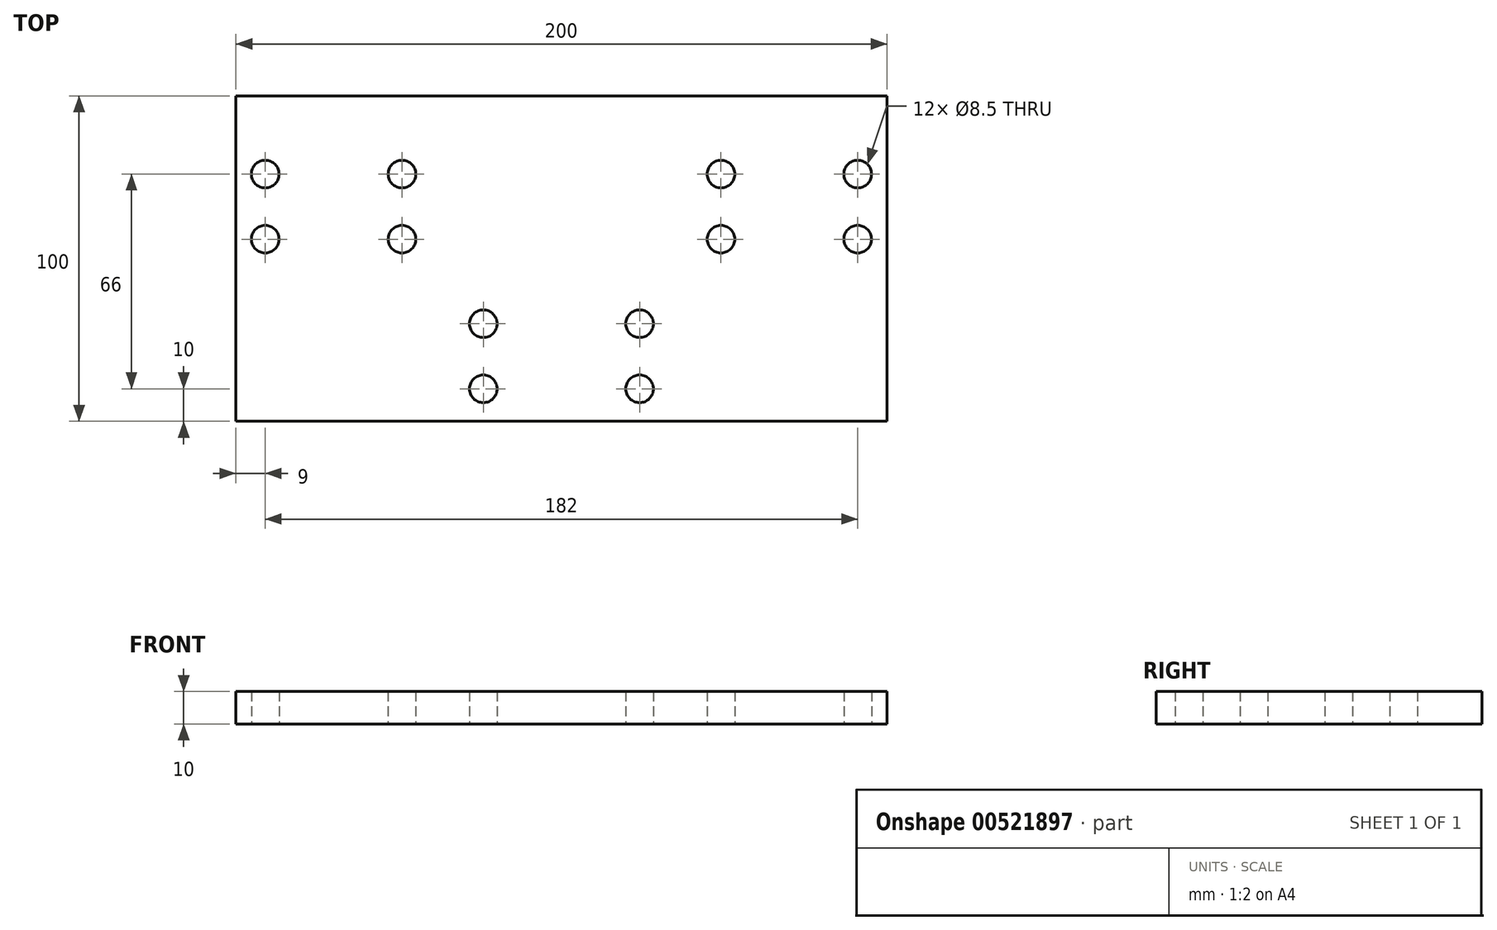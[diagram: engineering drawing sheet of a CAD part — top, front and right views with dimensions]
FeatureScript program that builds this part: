
annotation { "Feature Type Name" : "Feature", "Feature Type Description" : "" }
export const myFeature = defineFeature(function(context is Context, id is Id, definition is map)
    precondition{}
    {
        {
            var Q0;
            Q0=qCreatedBy(makeId("Top.planeOp"),FACE);
            var sketch = newSketch(context, id + "F0", { "sketchPlane" : qUnion([Q0])});
            skLineSegment(sketch, "E0.bottom", {"start": v(-100, 80) * mm, "end": v(100, 80) * mm});
            skLineSegment(sketch, "E0.top", {"start": v(-100, -20) * mm, "end": v(100, -20) * mm});
            skLineSegment(sketch, "E0.left", {"start": v(-100, 80) * mm, "end": v(-100, -20) * mm});
            skLineSegment(sketch, "E0.right", {"start": v(100, 80) * mm, "end": v(100, -20) * mm});
            skCircle(sketch, "E1", {"center": v(-70, 46) * mm, "radius": 12.5 * mm, "construction": true});
            skCircle(sketch, "E2", {"center": v(70, 46) * mm, "radius": 12.5 * mm, "construction": true});
            skCircle(sketch, "E3", {"center": v(0, 0) * mm, "radius": 15 * mm, "construction": true});
            skLineSegment(sketch, "E4", {"start": v(-70, 46) * mm, "end": v(70, 46) * mm, "construction": true});
            skCircle(sketch, "E5", {"center": v(-49, 56) * mm, "radius": 4.25 * mm});
            skCircle(sketch, "E6", {"center": v(-49, 36) * mm, "radius": 4.25 * mm});
            skCircle(sketch, "E7", {"center": v(-91, 36) * mm, "radius": 4.25 * mm});
            skCircle(sketch, "E8", {"center": v(-91, 56) * mm, "radius": 4.25 * mm});
            skCircle(sketch, "E9", {"center": v(49, 56) * mm, "radius": 4.25 * mm});
            skCircle(sketch, "E10", {"center": v(91, 56) * mm, "radius": 4.25 * mm});
            skCircle(sketch, "E11", {"center": v(49, 36) * mm, "radius": 4.25 * mm});
            skCircle(sketch, "E12", {"center": v(91, 36) * mm, "radius": 4.25 * mm});
            skLineSegment(sketch, "E13", {"start": v(-70, 46) * mm, "end": v(-70, 58.5) * mm, "construction": true});
            skLineSegment(sketch, "E14", {"start": v(70, 46) * mm, "end": v(70, 58.5) * mm, "construction": true});
            skCircle(sketch, "E15", {"center": v(-24, 10) * mm, "radius": 4.25 * mm});
            skCircle(sketch, "E16", {"center": v(-24, -10) * mm, "radius": 4.25 * mm});
            skCircle(sketch, "E17", {"center": v(24, -10) * mm, "radius": 4.25 * mm});
            skCircle(sketch, "E18", {"center": v(24, 10) * mm, "radius": 4.25 * mm});
            skLineSegment(sketch, "E19", {"start": v(0, 0) * mm, "end": v(-15, 0) * mm, "construction": true});
            skLineSegment(sketch, "E20", {"start": v(0, 0) * mm, "end": v(0, 15) * mm, "construction": true});
            skSolve(sketch);
        }
        {
            var Q0;
            Q0 = qSketchRegion(id + "F0", true);
            extrude(context, id + "F1", {"entities" : qUnion([Q0]), "depth" : 10 * mm, "offsetDistance" : 25 * mm});
        }
    });
